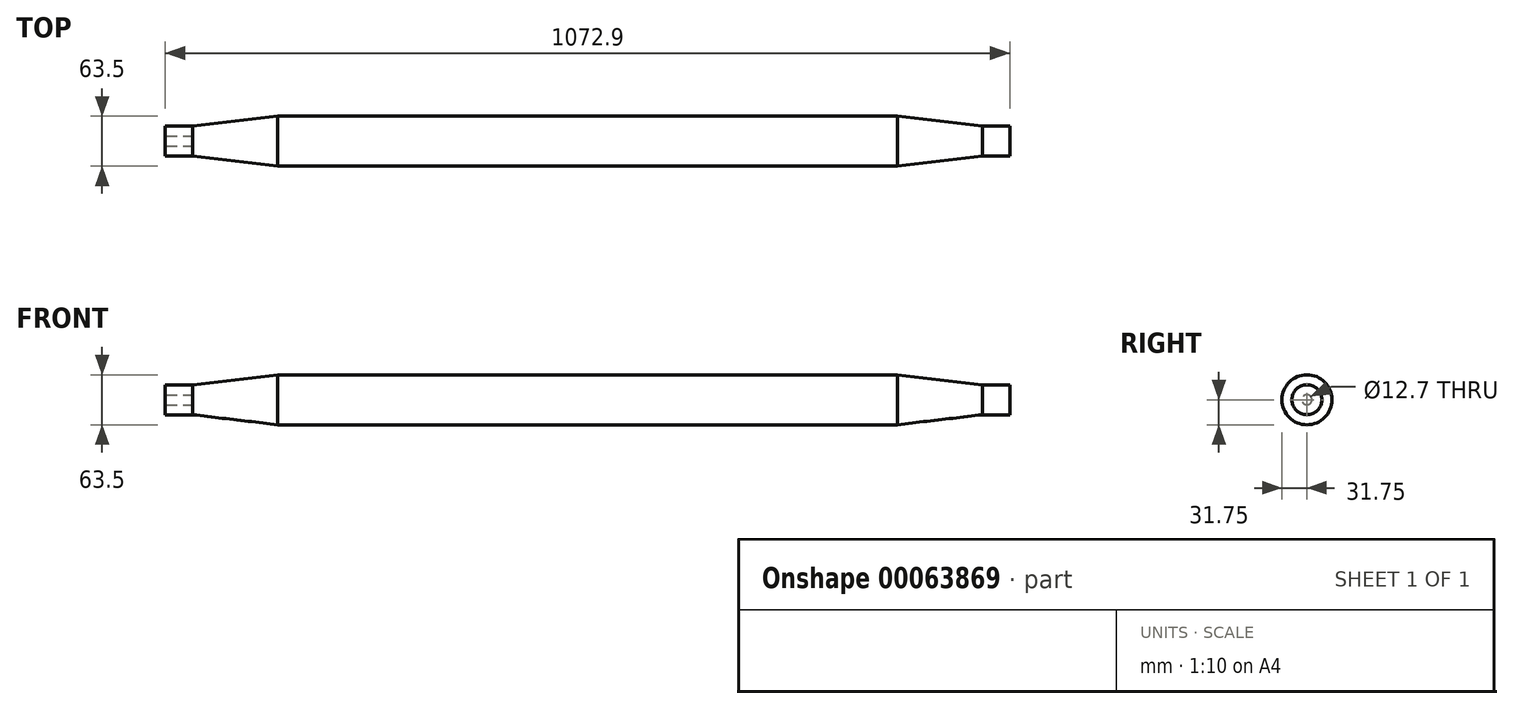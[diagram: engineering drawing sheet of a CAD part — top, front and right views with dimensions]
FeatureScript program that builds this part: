
annotation { "Feature Type Name" : "Feature", "Feature Type Description" : "" }
export const myFeature = defineFeature(function(context is Context, id is Id, definition is map)
    precondition{}
    {
        {
            var Q0;
            Q0=qCreatedBy(makeId("Right.planeOp"),FACE);
            var sketch = newSketch(context, id + "F0", { "sketchPlane" : qUnion([Q0])});
            skCircle(sketch, "E0", {"center": v(0, 0) * mm, "radius": 31.75 * mm});
            skSolve(sketch);
        }
        {
            var Q0;
            Q0 = qSketchRegion(id + "F0", true);
            extrude(context, id + "F1", {"entities" : qUnion([Q0]), "endBound" : BoundingType.SYMMETRIC, "depth" : 787.4 * mm});
        }
        {
            var Q0;
            Q0=makeQuery(id+"F1.opExtrude","CAP_FACE",FACE,{"disambiguationData":[OSD([sQuery(id+"F0.wireOp",EDGE,"E0")])],"isStart":false});
            cPlane(context, id + "F2", {"entities" : qUnion([Q0]), "cplaneType" : CPlaneType.OFFSET, "offset" : 142.75 * mm, "width" : 152.4 * mm, "height" : 152.4 * mm});
        }
        {
            var Q0;
            Q0=qCreatedBy(id+"F2.planeOp",FACE);
            var sketch = newSketch(context, id + "F3", { "sketchPlane" : qUnion([Q0])});
            skCircle(sketch, "E1", {"center": v(0, 0) * mm, "radius": 19.05 * mm});
            skSolve(sketch);
        }
        {
            var Q0;
            Q0 = qSketchRegion(id + "F3", true);
            extrude(context, id + "F4", {"entities" : qUnion([Q0]), "oppositeDirection" : true, "depth" : 35.05 * mm});
        }
        {
            var Q0;
            Q0=makeQuery(id+"F4.opExtrude","SWEPT_BODY",BODY,{"disambiguationData":[OSD([sQuery(id+"F3.wireOp",EDGE,"E1")])]});
            var Q1;
            Q1=qCreatedBy(makeId("Right.planeOp"),FACE);
            mirror(context, id + "F5", {"entities" : qUnion([Q0]), "mirrorPlane" : qUnion([Q1])});
        }
        {
            var Q0;
            Q0=makeQuery(id+"F1.opExtrude","CAP_FACE",FACE,{"disambiguationData":[OSD([sQuery(id+"F0.wireOp",EDGE,"E0")])],"isStart":false});
            var Q1;
            Q1=makeQuery(id+"F4.opExtrude","CAP_FACE",FACE,{"disambiguationData":[OSD([sQuery(id+"F3.wireOp",EDGE,"E1")])],"isStart":false});
            loft(context, id + "F6", {"sheetProfilesArray" : [{ "sheetProfileEntities" : qUnion([Q0]) }, { "sheetProfileEntities" : qUnion([Q1]) }]});
        }
        {
            var Q0;
            Q0=makeQuery(id+"F1.opExtrude","CAP_FACE",FACE,{"disambiguationData":[OSD([sQuery(id+"F0.wireOp",EDGE,"E0")])],"isStart":true});
            var Q1;
            Q1=makeQuery(id+"F5.opPattern","COPY",FACE,{"derivedFrom":makeQuery(id+"F4.opExtrude","CAP_FACE",FACE,{"disambiguationData":[OSD([sQuery(id+"F3.wireOp",EDGE,"E1")])],"isStart":false}),"instanceName":"1"});
            loft(context, id + "F7", {"sheetProfilesArray" : [{ "sheetProfileEntities" : qUnion([Q0]) }, { "sheetProfileEntities" : qUnion([Q1]) }]});
        }
        {
            var Q0;
            Q0=qCreatedBy(id+"F2.planeOp",FACE);
            var sketch = newSketch(context, id + "F8", { "sketchPlane" : qUnion([Q0])});
            skPoint(sketch, "E2", {"position": v(0, 0) * mm});
            skSolve(sketch);
        }
        {
            var Q0;
            Q0=sQuery(id+"F8.wireOp",VERTEX,"E2");
            var Q1;
            Q1=makeQuery(id+"F5.opPattern","COPY",BODY,{"derivedFrom":makeQuery(id+"F4.opExtrude","SWEPT_BODY",BODY,{"disambiguationData":[OSD([sQuery(id+"F3.wireOp",EDGE,"E1")])]}),"instanceName":"1"});
            hole(context, id + "F9", {"style" : HoleStyle.SIMPLE, "holeDiameter" : 12.7 * mm, "endStyle" : HoleEndStyle.BLIND, "holeDepth" : 44.45 * mm, "locations" : qUnion([Q0]), "scope" : qUnion([Q1])});
        }
        {
            var Q0;
            Q0=makeQuery(id+"F5.opPattern","COPY",FACE,{"derivedFrom":makeQuery(id+"F4.opExtrude","CAP_FACE",FACE,{"disambiguationData":[OSD([sQuery(id+"F3.wireOp",EDGE,"E1")])],"isStart":true}),"instanceName":"1"});
            var sketch = newSketch(context, id + "F10", { "sketchPlane" : qUnion([Q0])});
            skPoint(sketch, "E3", {"position": v(0, 0) * mm});
            skSolve(sketch);
        }
        {
            var Q0;
            Q0=sQuery(id+"F10.wireOp",VERTEX,"E3");
            var Q1;
            Q1=makeQuery(id+"F5.opPattern","COPY",BODY,{"derivedFrom":makeQuery(id+"F4.opExtrude","SWEPT_BODY",BODY,{"disambiguationData":[OSD([sQuery(id+"F3.wireOp",EDGE,"E1")])]}),"instanceName":"1"});
            hole(context, id + "F11", {"style" : HoleStyle.SIMPLE, "holeDiameter" : 12.7 * mm, "endStyle" : HoleEndStyle.BLIND, "holeDepth" : 44.45 * mm, "locations" : qUnion([Q0]), "scope" : qUnion([Q1])});
        }
    });
